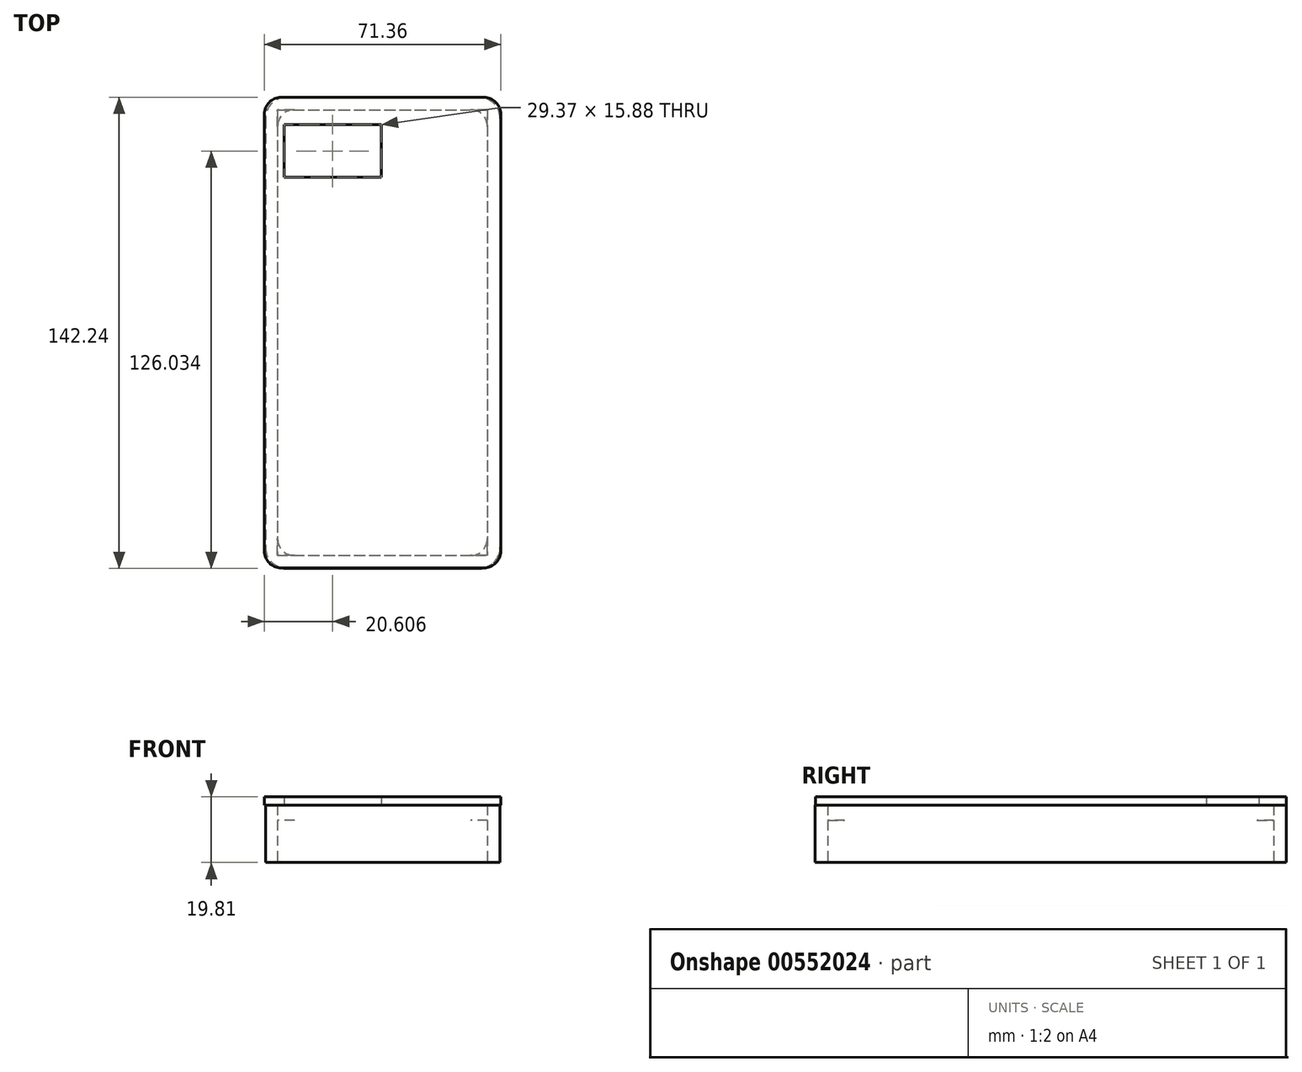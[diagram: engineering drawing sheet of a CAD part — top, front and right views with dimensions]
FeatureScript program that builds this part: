
annotation { "Feature Type Name" : "Feature", "Feature Type Description" : "" }
export const myFeature = defineFeature(function(context is Context, id is Id, definition is map)
    precondition{}
    {
        {
            var Q0;
            Q0=qCreatedBy(makeId("Top.planeOp"),FACE);
            var sketch = newSketch(context, id + "F0", { "sketchPlane" : qUnion([Q0])});
            skLineSegment(sketch, "E0.bottom", {"start": v(-29, 71.04) * mm, "end": v(29.15, 71.04) * mm});
            skLineSegment(sketch, "E0.top", {"start": v(-29, -71.2) * mm, "end": v(29.15, -71.2) * mm});
            skLineSegment(sketch, "E0.left", {"start": v(-35.35, 64.7) * mm, "end": v(-35.35, -64.85) * mm});
            skLineSegment(sketch, "E0.right", {"start": v(35.5, 64.7) * mm, "end": v(35.5, -64.85) * mm});
            skPoint(sketch, "E1.visualSharp", {"position": v(-35.35, 71.04) * mm});
            skArc(sketch, "E1.filletArc", {"start": v(-29, 71.04) * mm, "mid": v(-33.49, 69.19) * mm, "end": v(-35.35, 64.7) * mm});
            skPoint(sketch, "E2.visualSharp", {"position": v(35.5, 71.04) * mm});
            skArc(sketch, "E2.filletArc", {"start": v(35.5, 64.7) * mm, "mid": v(33.64, 69.19) * mm, "end": v(29.15, 71.04) * mm});
            skPoint(sketch, "E3.visualSharp", {"position": v(35.5, -71.2) * mm});
            skArc(sketch, "E3.filletArc", {"start": v(29.15, -71.2) * mm, "mid": v(33.64, -69.34) * mm, "end": v(35.5, -64.85) * mm});
            skPoint(sketch, "E4.visualSharp", {"position": v(-35.35, -71.2) * mm});
            skArc(sketch, "E4.filletArc", {"start": v(-35.35, -64.85) * mm, "mid": v(-33.49, -69.34) * mm, "end": v(-29, -71.2) * mm});
            skLineSegment(sketch, "E5.bottom", {"start": v(-31.67, 67.3) * mm, "end": v(31.67, 67.3) * mm});
            skLineSegment(sketch, "E5.top", {"start": v(-31.67, -67.3) * mm, "end": v(31.67, -67.3) * mm});
            skLineSegment(sketch, "E5.left", {"start": v(-31.67, 67.3) * mm, "end": v(-31.67, -67.3) * mm});
            skLineSegment(sketch, "E5.right", {"start": v(31.67, 67.3) * mm, "end": v(31.67, -67.3) * mm});
            skPoint(sketch, "E5.middle", {"position": v(0, 0) * mm});
            skLineSegment(sketch, "E6", {"start": v(26.95, 66.57) * mm, "end": v(4.13, 66.57) * mm});
            skLineSegment(sketch, "E7", {"start": v(4.13, 66.57) * mm, "end": v(-3.38, 66.57) * mm});
            skLineSegment(sketch, "E8", {"start": v(-3.38, 66.57) * mm, "end": v(-3.38, 50.06) * mm});
            skLineSegment(sketch, "E9", {"start": v(-3.38, 50.06) * mm, "end": v(31.45, 50.06) * mm});
            skLineSegment(sketch, "E10", {"start": v(31.45, 50.06) * mm, "end": v(31.45, 66.57) * mm});
            skLineSegment(sketch, "E11", {"start": v(31.45, 66.57) * mm, "end": v(26.95, 66.57) * mm});
            skSolve(sketch);
        }
        {
            var Q0;
            Q0 = qSketchRegion(id + "F0", true);
            extrude(context, id + "F1", {"entities" : qUnion([Q0]), "depth" : 12.7 * mm, "offsetDistance" : 25.4 * mm});
        }
        {
            var Q0;
            Q0=makeQuery(id+"F1.opExtrude","SWEPT_EDGE",EDGE,{"disambiguationData":[OSD([sQuery(id+"F0.wireOp",EDGE,"E5.bottom"),sQuery(id+"F0.wireOp",EDGE,"E5.left")])]});
            var Q1;
            Q1=makeQuery(id+"F1.opExtrude","SWEPT_EDGE",EDGE,{"disambiguationData":[OSD([sQuery(id+"F0.wireOp",EDGE,"E5.bottom"),sQuery(id+"F0.wireOp",EDGE,"E5.right")])]});
            var Q2;
            Q2=makeQuery(id+"F1.opExtrude","SWEPT_EDGE",EDGE,{"disambiguationData":[OSD([sQuery(id+"F0.wireOp",EDGE,"E5.top"),sQuery(id+"F0.wireOp",EDGE,"E5.right")])]});
            var Q3;
            Q3=makeQuery(id+"F1.opExtrude","SWEPT_EDGE",EDGE,{"disambiguationData":[OSD([sQuery(id+"F0.wireOp",EDGE,"E5.top"),sQuery(id+"F0.wireOp",EDGE,"E5.left")])]});
            fillet(context, id + "F2", {"entities" : qUnion([Q0, Q1, Q2, Q3]), "radius" : 5.08 * mm, "tangentPropagation" : true, "allowEdgeOverflow" : false});
        }
        {
            var Q0;
            Q0 = qSketchRegion(id + "F0", true);
            extrude(context, id + "F3", {"entities" : qUnion([Q0]), "operationType" : NewBodyOperationType.ADD, "depth" : 17.27 * mm, "offsetDistance" : 25.4 * mm});
        }
        {
            var Q0;
            Q0=makeQuery(id+"F3.opExtrude","CAP_FACE",FACE,{"disambiguationData":[OSD([sQuery(id+"F0.wireOp",EDGE,"E0.bottom"),sQuery(id+"F0.wireOp",EDGE,"E0.top"),sQuery(id+"F0.wireOp",EDGE,"E0.left"),sQuery(id+"F0.wireOp",EDGE,"E0.right"),sQuery(id+"F0.wireOp",EDGE,"E1.filletArc"),sQuery(id+"F0.wireOp",EDGE,"E2.filletArc"),sQuery(id+"F0.wireOp",EDGE,"E3.filletArc"),sQuery(id+"F0.wireOp",EDGE,"E4.filletArc"),sQuery(id+"F0.wireOp",EDGE,"E5.bottom"),sQuery(id+"F0.wireOp",EDGE,"E5.top"),sQuery(id+"F0.wireOp",EDGE,"E5.left"),sQuery(id+"F0.wireOp",EDGE,"E5.right")])],"isStart":false});
            var sketch = newSketch(context, id + "F4", { "sketchPlane" : qUnion([Q0])});
            skLineSegment(sketch, "E12.bottom", {"start": v(-35.68, 71.04) * mm, "end": v(35.68, 71.04) * mm});
            skLineSegment(sketch, "E12.top", {"start": v(-35.68, -71.04) * mm, "end": v(35.68, -71.04) * mm});
            skLineSegment(sketch, "E12.left", {"start": v(-35.68, 71.04) * mm, "end": v(-35.68, -71.04) * mm});
            skLineSegment(sketch, "E12.right", {"start": v(35.68, 71.04) * mm, "end": v(35.68, -71.04) * mm});
            skPoint(sketch, "E12.middle", {"position": v(0, 0) * mm});
            skLineSegment(sketch, "E13.bottom", {"start": v(-29.76, 62.77) * mm, "end": v(-0.4, 62.77) * mm});
            skLineSegment(sketch, "E13.top", {"start": v(-29.76, 46.9) * mm, "end": v(-0.4, 46.9) * mm});
            skLineSegment(sketch, "E13.left", {"start": v(-29.76, 62.77) * mm, "end": v(-29.76, 46.9) * mm});
            skLineSegment(sketch, "E13.right", {"start": v(-0.4, 62.77) * mm, "end": v(-0.4, 46.9) * mm});
            skSolve(sketch);
        }
        {
            var Q0;
            Q0 = qSketchRegion(id + "F4", true);
            extrude(context, id + "F5", {"entities" : qUnion([Q0]), "operationType" : NewBodyOperationType.ADD, "depth" : 2.54 * mm, "offsetDistance" : 25.4 * mm});
        }
        {
            var Q0;
            Q0=makeQuery(id+"F5.opExtrude","SWEPT_EDGE",EDGE,{"disambiguationData":[OSD([sQuery(id+"F4.wireOp",EDGE,"E12.bottom"),sQuery(id+"F4.wireOp",EDGE,"E12.left")])]});
            var Q1;
            Q1=makeQuery(id+"F5.opExtrude","SWEPT_EDGE",EDGE,{"disambiguationData":[OSD([sQuery(id+"F4.wireOp",EDGE,"E12.bottom"),sQuery(id+"F4.wireOp",EDGE,"E12.right")])]});
            var Q2;
            Q2=makeQuery(id+"F5.opExtrude","SWEPT_EDGE",EDGE,{"disambiguationData":[OSD([sQuery(id+"F4.wireOp",EDGE,"E12.top"),sQuery(id+"F4.wireOp",EDGE,"E12.right")])]});
            var Q3;
            Q3=makeQuery(id+"F5.opExtrude","SWEPT_EDGE",EDGE,{"disambiguationData":[OSD([sQuery(id+"F4.wireOp",EDGE,"E12.top"),sQuery(id+"F4.wireOp",EDGE,"E12.left")])]});
            fillet(context, id + "F6", {"entities" : qUnion([Q0, Q1, Q2, Q3]), "radius" : 5.08 * mm, "tangentPropagation" : true, "allowEdgeOverflow" : false});
        }
    });
